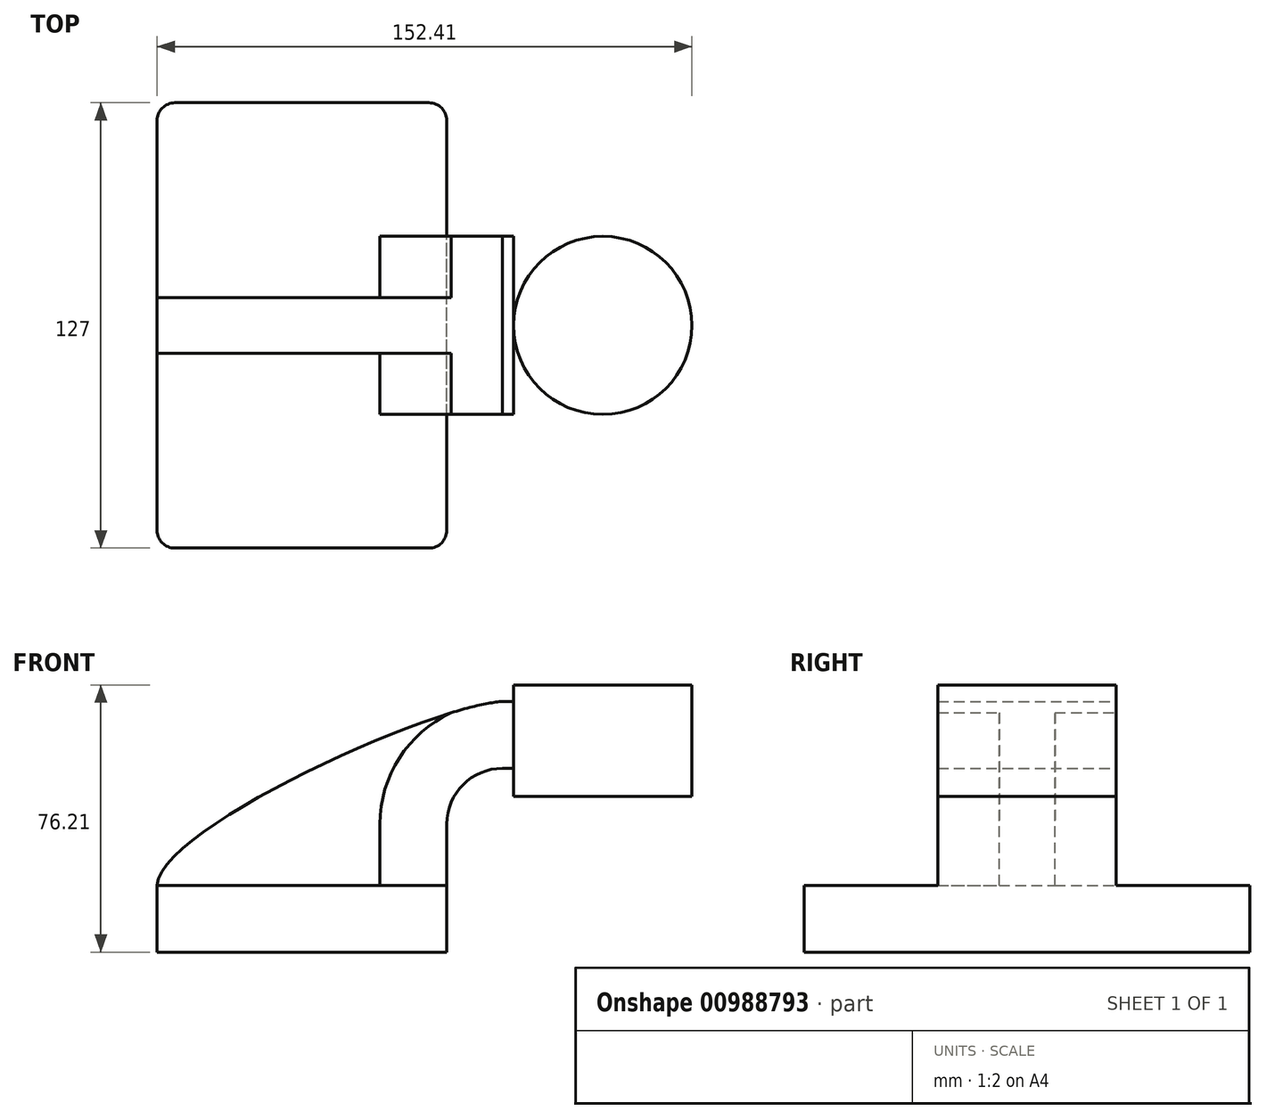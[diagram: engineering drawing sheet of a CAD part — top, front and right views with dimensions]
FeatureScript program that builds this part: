
annotation { "Feature Type Name" : "Feature", "Feature Type Description" : "" }
export const myFeature = defineFeature(function(context is Context, id is Id, definition is map)
    precondition{}
    {
        {
            var Q0;
            Q0=qCreatedBy(makeId("Front.planeOp"),FACE);
            var sketch = newSketch(context, id + "F0", { "sketchPlane" : qUnion([Q0])});
            skLineSegment(sketch, "E0.bottom", {"start": v(-41.28, 9.52) * mm, "end": v(41.27, 9.53) * mm});
            skLineSegment(sketch, "E0.top", {"start": v(-41.28, -9.53) * mm, "end": v(41.28, -9.53) * mm});
            skLineSegment(sketch, "E0.left", {"start": v(-41.28, 9.52) * mm, "end": v(-41.27, -9.53) * mm});
            skLineSegment(sketch, "E0.right", {"start": v(41.28, 9.53) * mm, "end": v(41.28, -9.52) * mm});
            skPoint(sketch, "E0.middle", {"position": v(0, 0) * mm});
            skLineSegment(sketch, "E1.bottom", {"start": v(60.32, 66.68) * mm, "end": v(111.12, 66.68) * mm});
            skLineSegment(sketch, "E1.top", {"start": v(60.33, 34.93) * mm, "end": v(111.12, 34.93) * mm});
            skLineSegment(sketch, "E1.left", {"start": v(60.32, 66.68) * mm, "end": v(60.33, 34.93) * mm});
            skLineSegment(sketch, "E1.right", {"start": v(111.12, 66.68) * mm, "end": v(111.12, 34.93) * mm});
            skPoint(sketch, "E1.middle", {"position": v(85.72, 50.8) * mm});
            skLineSegment(sketch, "E2", {"start": v(41.27, 9.53) * mm, "end": v(41.27, 27) * mm});
            skArc(sketch, "E3", {"start": v(41.27, 27) * mm, "mid": v(45.92, 38.23) * mm, "end": v(57.15, 42.88) * mm});
            skLineSegment(sketch, "E4", {"start": v(57.15, 42.88) * mm, "end": v(85.72, 42.88) * mm});
            skLineSegment(sketch, "E5.0", {"start": v(57.15, 61.93) * mm, "end": v(85.72, 61.93) * mm});
            skArc(sketch, "E5.1", {"start": v(22.22, 27) * mm, "mid": v(32.45, 51.7) * mm, "end": v(57.15, 61.93) * mm});
            skLineSegment(sketch, "E5.2", {"start": v(22.23, 9.53) * mm, "end": v(22.23, 27) * mm});
            skFitSpline(sketch, "E6", {"points": [v(-41.28, 9.53) * mm, v(57.15, 61.93) * mm], "startDerivative": vector(2.75, 49.67) * mm, "endDerivative": vector(59.89, 2.94) * mm});
            skLineSegment(sketch, "E7", {"start": v(85.72, 34.93) * mm, "end": v(85.72, 66.68) * mm});
            skSolve(sketch);
        }
        {
            var Q0;
            Q0=makeQuery(id+"F0.imprint","IMPRINT",FACE,{"disambiguationData":[TD([[makeQuery(id+"F0.imprint","IMPRINT",EDGE,{"derivedFrom":sQuery(id+"F0.wireOp",EDGE,"E0.top")}),1.0]])]});
            extrude(context, id + "F1", {"entities" : qUnion([Q0]), "depth" : 127 * mm, "offsetDistance" : 25.4 * mm, "symmetric" : true});
        }
        {
            var Q0;
            {var subQ6=sQuery(id+"F0.wireOp",EDGE,"E2");Q0=makeQuery(id+"F0.imprint","IMPRINT",FACE,{"disambiguationData":[TD([[makeQuery(id+"F0.imprint","IMPRINT",EDGE,{"derivedFrom":subQ6}),1.0]])]});}
            extrude(context, id + "F2", {"entities" : qUnion([Q0]), "operationType" : NewBodyOperationType.ADD, "depth" : 50.8 * mm, "offsetDistance" : 25.4 * mm, "symmetric" : true});
        }
        {
            var Q0;
            {var subQ3=sQuery(id+"F0.wireOp",EDGE,"E5.2");Q0=makeQuery(id+"F0.imprint","IMPRINT",FACE,{"disambiguationData":[TD([[makeQuery(id+"F0.imprint","IMPRINT",EDGE,{"derivedFrom":subQ3}),1.0]])]});}
            extrude(context, id + "F3", {"entities" : qUnion([Q0]), "operationType" : NewBodyOperationType.ADD, "depth" : 15.88 * mm, "offsetDistance" : 25.4 * mm, "symmetric" : true});
        }
        {
            var Q0;
            {var subQ4=sQuery(id+"F0.wireOp",EDGE,"E1.right");Q0=makeQuery(id+"F0.imprint","IMPRINT",FACE,{"disambiguationData":[TD([[makeQuery(id+"F0.imprint","IMPRINT",EDGE,{"derivedFrom":subQ4}),-1.0]])]});}
            var Q1;
            Q1=sQuery(id+"F0.wireOp",EDGE,"E7");
            revolve(context, id + "F4", {"operationType" : NewBodyOperationType.ADD, "surfaceOperationType" : NewSurfaceOperationType.NEW, "entities" : qUnion([Q0]), "axis" : qUnion([Q1]), "revolveType" : RevolveType.FULL});
        }
        {
            var Q0;
            Q0=makeQuery(id+"F1.opExtrude","CAP_EDGE",EDGE,{"disambiguationData":[OSD([sQuery(id+"F0.wireOp",EDGE,"E0.left")])],"isStart":false});
            var Q1;
            Q1=makeQuery(id+"F1.opExtrude","CAP_EDGE",EDGE,{"disambiguationData":[OSD([sQuery(id+"F0.wireOp",EDGE,"E0.right")])],"isStart":false});
            var Q2;
            Q2=makeQuery(id+"F1.opExtrude","CAP_EDGE",EDGE,{"disambiguationData":[OSD([sQuery(id+"F0.wireOp",EDGE,"E0.left")])],"isStart":true});
            var Q3;
            Q3=makeQuery(id+"F1.opExtrude","CAP_EDGE",EDGE,{"disambiguationData":[OSD([sQuery(id+"F0.wireOp",EDGE,"E0.right")])],"isStart":true});
            fillet(context, id + "F5", {"entities" : qUnion([Q0, Q1, Q2, Q3]), "radius" : 5.08 * mm, "tangentPropagation" : true, "allowEdgeOverflow" : false});
        }
    });
